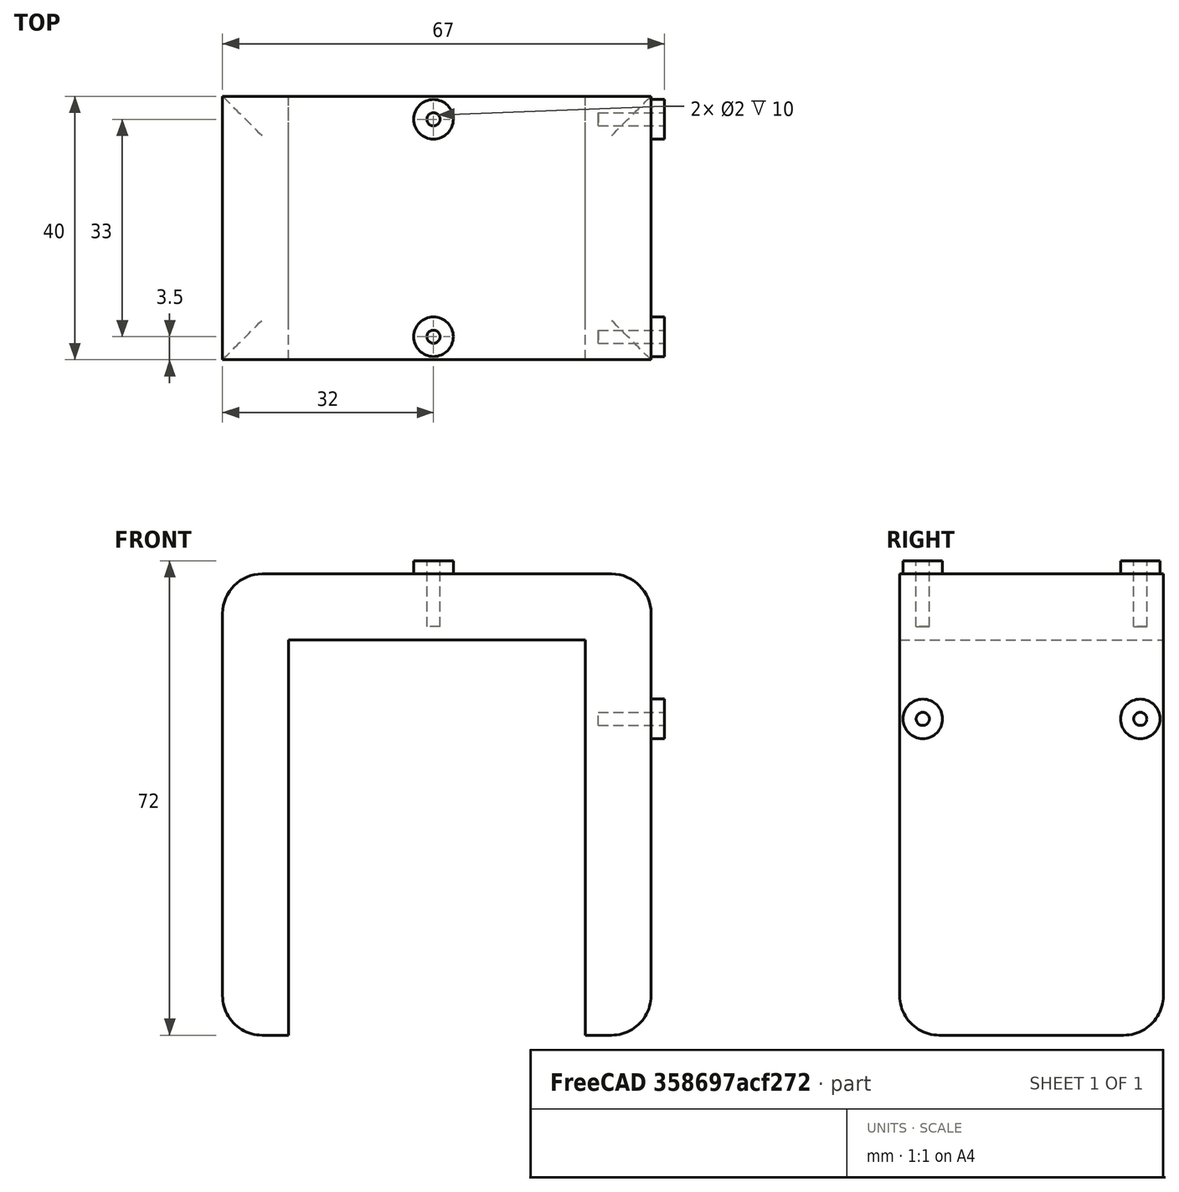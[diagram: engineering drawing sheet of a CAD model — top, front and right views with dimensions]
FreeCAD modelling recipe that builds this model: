
FCSTD DOCUMENT  (FreeCAD 0.18.4R)
Label: supporto-webcam-culla
License: All rights reserved
LicenseURL: http://en.wikipedia.org/wiki/All_rights_reserved
objects: Part::Cylinder×8, Part::Cut×4, Part::Box×3, Part::MultiFuse×1, Part::Fillet×1
note: 17 computed .brp shape members not serialized (recipe doc carries the construction recipe); baked Part::Feature solids carry a one-line shape summary decoded from their .brp

FEATURE [Part::Box] Box  label="Cube"
  AttacherType = Attacher::AttachEngine3D
  Height = 70
  Length = 10
  Placement = pos=(-10,0,0) rot=(0,0,1;0rad)
  Width = 40
FEATURE [Part::Box] Box001  label="Cube001"
  AttacherType = Attacher::AttachEngine3D
  Height = 70
  Length = 10
  Placement = pos=(45,0,0) rot=(0,0,1;0rad)
  Width = 40
FEATURE [Part::Box] Box002  label="Cube002"
  AttacherType = Attacher::AttachEngine3D
  Height = 10
  Length = 45
  Placement = pos=(0,0,60) rot=(0,0,1;0rad)
  Width = 40
FEATURE [Part::Cylinder] Cylinder010
  Angle = 360
  AttacherType = Attacher::AttachEngine3D
  Height = 10
  Placement = pos=(47,3.5,48) rot=(0,1,0;1.5708rad)
  Radius = 3
FEATURE [Part::Cylinder] Cylinder011  label="foro"
  Angle = 360
  AttacherType = Attacher::AttachEngine3D
  Height = 10
  Placement = pos=(47,3.5,48) rot=(0,1,0;1.5708rad)
  Radius = 1
FEATURE [Part::Cylinder] Cylinder012
  Angle = 360
  AttacherType = Attacher::AttachEngine3D
  Height = 10
  Placement = pos=(47,36.5,48) rot=(0,1,0;1.5708rad)
  Radius = 3
FEATURE [Part::Cylinder] Cylinder013  label="foro001"
  Angle = 360
  AttacherType = Attacher::AttachEngine3D
  Height = 10
  Placement = pos=(47,36.5,48) rot=(0,1,0;1.5708rad)
  Radius = 1
FEATURE [Part::Cylinder] Cylinder014  label="foro002"
  Angle = 360
  AttacherType = Attacher::AttachEngine3D
  Height = 10
  Placement = pos=(22,36.5,62) rot=(0,0,1;0rad)
  Radius = 1
FEATURE [Part::Cylinder] Cylinder015
  Angle = 360
  AttacherType = Attacher::AttachEngine3D
  Height = 10
  Placement = pos=(22,36.5,62) rot=(0,0,1;0rad)
  Radius = 3
FEATURE [Part::Cylinder] Cylinder016
  Angle = 360
  AttacherType = Attacher::AttachEngine3D
  Height = 10
  Placement = pos=(22,3.5,62) rot=(0,0,1;0rad)
  Radius = 3
FEATURE [Part::Cylinder] Cylinder017  label="foro003"
  Angle = 360
  AttacherType = Attacher::AttachEngine3D
  Height = 10
  Placement = pos=(22,3.5,62) rot=(0,0,1;0rad)
  Radius = 1
FEATURE [Part::MultiFuse] Fusion
  Shapes = -> [Box002,Box001,Cylinder016,Cylinder015,Cylinder012,Cylinder010,Box]
FEATURE [Part::Cut] Cut
  Base = -> Fusion
  Tool = -> Cylinder011
FEATURE [Part::Cut] Cut001
  Base = -> Cut
  Tool = -> Cylinder017
FEATURE [Part::Cut] Cut002
  Base = -> Cut001
  Tool = -> Cylinder014
FEATURE [Part::Cut] Cut003
  Base = -> Cut002
  Tool = -> Cylinder013
FEATURE [Part::Fillet] Fillet
  Base = -> Cut003
  Edges = 8 edges r=6: [Edge8,Edge17,Edge27,Edge28,Edge29,Edge34,Edge40,Edge41]
